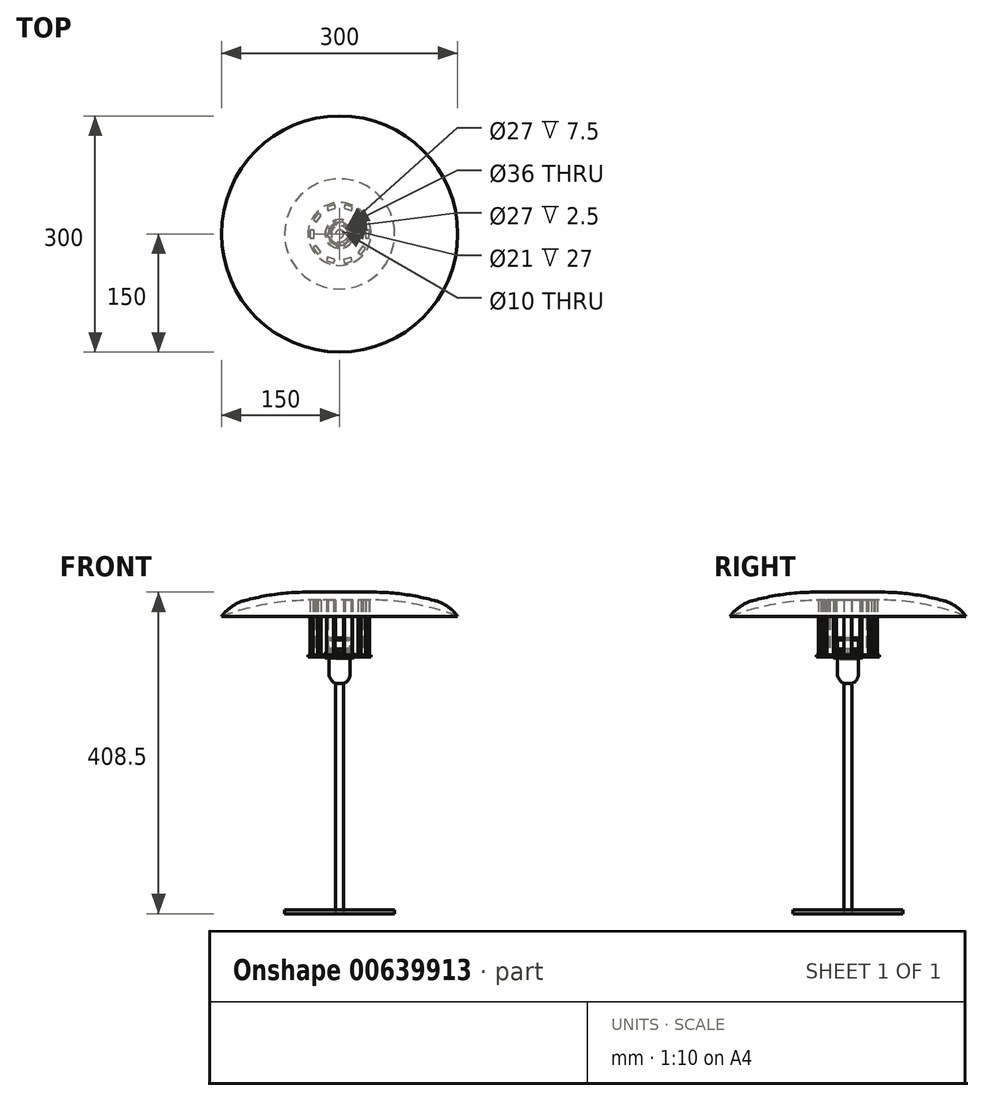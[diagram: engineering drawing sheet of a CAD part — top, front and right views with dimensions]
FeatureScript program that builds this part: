
annotation { "Feature Type Name" : "Feature", "Feature Type Description" : "" }
export const myFeature = defineFeature(function(context is Context, id is Id, definition is map)
    precondition{}
    {
        {
            var Q0;
            Q0=qCreatedBy(makeId("Top.planeOp"),FACE);
            var sketch = newSketch(context, id + "F0", { "sketchPlane" : qUnion([Q0])});
            skCircle(sketch, "E0", {"center": v(0, 0) * mm, "radius": 70 * mm});
            skSolve(sketch);
        }
        {
            var Q0;
            Q0=makeQuery(id+"F0.imprint","IMPRINT",FACE,{"disambiguationData":[TD([[makeQuery(id+"F0.imprint","IMPRINT",EDGE,{"derivedFrom":sQuery(id+"F0.wireOp",EDGE,"E0")}),1.0]])]});
            extrude(context, id + "F1", {"entities" : qUnion([Q0]), "depth" : 5 * mm, "offsetDistance" : 25 * mm});
        }
        {
            var Q0;
            Q0=makeQuery(id+"F1.opExtrude","CAP_FACE",FACE,{"disambiguationData":[OSD([sQuery(id+"F0.wireOp",EDGE,"E0")])],"isStart":false});
            var sketch = newSketch(context, id + "F2", { "sketchPlane" : qUnion([Q0])});
            skCircle(sketch, "E1", {"center": v(0, 0) * mm, "radius": 5 * mm});
            skSolve(sketch);
        }
        {
            var Q0;
            Q0=makeQuery(id+"F2.imprint","IMPRINT",FACE,{"disambiguationData":[TD([[makeQuery(id+"F2.imprint","IMPRINT",EDGE,{"derivedFrom":sQuery(id+"F2.wireOp",EDGE,"E1")}),1.0]])]});
            extrude(context, id + "F3", {"entities" : qUnion([Q0]), "operationType" : NewBodyOperationType.REMOVE, "endBound" : BoundingType.UP_TO_NEXT, "oppositeDirection" : true, "depth" : 25 * mm, "offsetDistance" : 25 * mm});
        }
        {
            var Q0;
            Q0=qCreatedBy(makeId("Top.planeOp"),FACE);
            var sketch = newSketch(context, id + "F4", { "sketchPlane" : qUnion([Q0])});
            skCircle(sketch, "E2", {"center": v(0, 0) * mm, "radius": 5 * mm});
            skSolve(sketch);
        }
        {
            var Q0;
            Q0=makeQuery(id+"F4.imprint","IMPRINT",FACE,{"disambiguationData":[TD([[makeQuery(id+"F4.imprint","IMPRINT",EDGE,{"derivedFrom":sQuery(id+"F4.wireOp",EDGE,"E2")}),1.0]])]});
            extrude(context, id + "F5", {"entities" : qUnion([Q0]), "depth" : 350 * mm, "offsetDistance" : 25 * mm});
        }
        {
            var Q0;
            Q0=qCreatedBy(makeId("Front.planeOp"),FACE);
            var sketch = newSketch(context, id + "F6", { "sketchPlane" : qUnion([Q0])});
            skLineSegment(sketch, "E3", {"start": v(0, 350) * mm, "end": v(13.5, 350) * mm});
            skLineSegment(sketch, "E4", {"start": v(13.5, 350) * mm, "end": v(13.5, 330.63) * mm});
            skLineSegment(sketch, "E5", {"start": v(13.5, 330.63) * mm, "end": v(13.5, 326) * mm});
            skLineSegment(sketch, "E6", {"start": v(13.5, 326) * mm, "end": v(18.5, 326) * mm});
            skLineSegment(sketch, "E7", {"start": v(18.5, 326) * mm, "end": v(18.5, 325) * mm});
            skLineSegment(sketch, "E8", {"start": v(18.5, 325) * mm, "end": v(13.5, 325) * mm});
            skLineSegment(sketch, "E9", {"start": v(13.5, 325) * mm, "end": v(13.5, 305) * mm});
            skArc(sketch, "E10", {"start": v(0, 291.5) * mm, "mid": v(9.55, 295.45) * mm, "end": v(13.5, 305) * mm});
            skLineSegment(sketch, "E11", {"start": v(0, 350) * mm, "end": v(0, 291.5) * mm});
            skSolve(sketch);
        }
        {
            var Q0;
            Q0=makeQuery(id+"F6.imprint","IMPRINT",FACE,{"disambiguationData":[TD([[makeQuery(id+"F6.imprint","IMPRINT",EDGE,{"derivedFrom":sQuery(id+"F6.wireOp",EDGE,"E3")}),-1.0]])]});
            var Q1;
            Q1=sQuery(id+"F6.wireOp",EDGE,"E11");
            revolve(context, id + "F7", {"operationType" : NewBodyOperationType.ADD, "entities" : qUnion([Q0]), "axis" : qUnion([Q1]), "revolveType" : RevolveType.FULL});
        }
        {
            var Q0;
            Q0=makeQuery(id+"F7.opRevolve","SWEPT_EDGE",EDGE,{"disambiguationData":[OSD([sQuery(id+"F6.wireOp",EDGE,"E6"),sQuery(id+"F6.wireOp",EDGE,"E7")])]});
            fillet(context, id + "F8", {"entities" : qUnion([Q0]), "radius" : 0.5 * mm, "tangentPropagation" : true, "allowEdgeOverflow" : false});
        }
        {
            var Q0;
            Q0=makeQuery(id+"F7.opRevolve","SWEPT_EDGE",EDGE,{"disambiguationData":[OSD([sQuery(id+"F6.wireOp",EDGE,"E7"),sQuery(id+"F6.wireOp",EDGE,"E8")])]});
            fillet(context, id + "F9", {"entities" : qUnion([Q0]), "radius" : 0.5 * mm, "tangentPropagation" : true, "allowEdgeOverflow" : false});
        }
        {
            var Q0;
            Q0=makeQuery(id+"F7.opRevolve","SWEPT_EDGE",EDGE,{"disambiguationData":[OSD([sQuery(id+"F6.wireOp",EDGE,"E3"),sQuery(id+"F6.wireOp",EDGE,"E4")])]});
            chamfer(context, id + "F10", {"entities" : qUnion([Q0]), "chamferType" : ChamferType.TWO_OFFSETS, "width1" : 1 * mm, "oppositeDirection" : false, "width2" : 2 * mm, "tangentPropagation" : true});
        }
        {
            var Q0;
            Q0=makeQuery(id+"F7.boolean.opBoolean","MERGE",FACE,{"derivedFrom":[makeQuery(id+"F5.opExtrude","CAP_FACE",FACE,{"disambiguationData":[OSD([sQuery(id+"F4.wireOp",EDGE,"E2")])],"isStart":false}),makeQuery(id+"F7.opRevolve","SWEPT_FACE",FACE,{"disambiguationData":[OSD([sQuery(id+"F6.wireOp",EDGE,"E3")])]})]});
            var sketch = newSketch(context, id + "F11", { "sketchPlane" : qUnion([Q0])});
            skCircle(sketch, "E12", {"center": v(0, 0) * mm, "radius": 10.5 * mm});
            skSolve(sketch);
        }
        {
            var Q0;
            Q0=makeQuery(id+"F11.imprint","IMPRINT",FACE,{"disambiguationData":[TD([[makeQuery(id+"F11.imprint","IMPRINT",EDGE,{"derivedFrom":sQuery(id+"F11.wireOp",EDGE,"E12")}),1.0]])]});
            extrude(context, id + "F12", {"entities" : qUnion([Q0]), "operationType" : NewBodyOperationType.REMOVE, "oppositeDirection" : true, "depth" : 27 * mm, "offsetDistance" : 25 * mm});
        }
        {
            var Q0;
            Q0=qCreatedBy(makeId("Front.planeOp"),FACE);
            var sketch = newSketch(context, id + "F13", { "sketchPlane" : qUnion([Q0])});
            skLineSegment(sketch, "E13", {"start": v(18, 329) * mm, "end": v(18, 331.5) * mm});
            skLineSegment(sketch, "E14", {"start": v(18, 331.5) * mm, "end": v(15.5, 331.5) * mm});
            skLineSegment(sketch, "E15", {"start": v(15.5, 331.5) * mm, "end": v(15.5, 336.5) * mm});
            skLineSegment(sketch, "E16", {"start": v(15.5, 336.5) * mm, "end": v(13.5, 336.5) * mm});
            skLineSegment(sketch, "E17", {"start": v(13.5, 336.5) * mm, "end": v(13.5, 329) * mm});
            skLineSegment(sketch, "E18", {"start": v(13.5, 329) * mm, "end": v(18, 329) * mm});
            skLineSegment(sketch, "E19", {"start": v(0, 351.5) * mm, "end": v(0, 305.84) * mm, "construction": true});
            skSolve(sketch);
        }
        {
            var Q0;
            Q0=makeQuery(id+"F13.imprint","IMPRINT",FACE,{"disambiguationData":[TD([[makeQuery(id+"F13.imprint","IMPRINT",EDGE,{"derivedFrom":sQuery(id+"F13.wireOp",EDGE,"E13")}),1.0]])]});
            var Q1;
            Q1=sQuery(id+"F13.wireOp",EDGE,"E19");
            revolve(context, id + "F14", {"entities" : qUnion([Q0]), "axis" : qUnion([Q1]), "revolveType" : RevolveType.FULL});
        }
        {
            var Q0;
            Q0=makeQuery(id+"F14.opRevolve","SWEPT_FACE",FACE,{"disambiguationData":[OSD([sQuery(id+"F13.wireOp",EDGE,"E16")])]});
            var sketch = newSketch(context, id + "F15", { "sketchPlane" : qUnion([Q0])});
            skArc(sketch, "E20", {"start": v(-15.5, 0) * mm, "mid": v(-15.16, 3.22) * mm, "end": v(-14.16, 6.3) * mm});
            skLineSegment(sketch, "E21", {"start": v(-14.16, 6.3) * mm, "end": v(0, 0) * mm});
            skLineSegment(sketch, "E22", {"start": v(-15.5, 0) * mm, "end": v(0, 0) * mm});
            skArc(sketch, "E23", {"start": v(-13.25, 5.9) * mm, "mid": v(-14.18, 3.01) * mm, "end": v(-14.5, 0) * mm});
            skArc(sketch, "E24.1.0", {"start": v(-14.18, -3.01) * mm, "mid": v(-13.25, -5.9) * mm, "end": v(-11.73, -8.52) * mm});
            skArc(sketch, "E24.1.1", {"start": v(-12.54, -9.11) * mm, "mid": v(-14.16, -6.3) * mm, "end": v(-15.16, -3.22) * mm});
            skLineSegment(sketch, "E24.1.2", {"start": v(-15.16, -3.22) * mm, "end": v(0, 0) * mm});
            skLineSegment(sketch, "E24.1.3", {"start": v(-12.54, -9.11) * mm, "end": v(0, 0) * mm});
            skArc(sketch, "E24.2.0", {"start": v(-9.7, -10.78) * mm, "mid": v(-7.25, -12.56) * mm, "end": v(-4.48, -13.8) * mm});
            skArc(sketch, "E24.2.1", {"start": v(-4.79, -14.74) * mm, "mid": v(-7.75, -13.42) * mm, "end": v(-10.37, -11.52) * mm});
            skLineSegment(sketch, "E24.2.2", {"start": v(-10.37, -11.52) * mm, "end": v(0, 0) * mm});
            skLineSegment(sketch, "E24.2.3", {"start": v(-4.79, -14.74) * mm, "end": v(0, 0) * mm});
            skArc(sketch, "E24.3.0", {"start": v(-1.52, -14.42) * mm, "mid": v(1.52, -14.42) * mm, "end": v(4.48, -13.8) * mm});
            skArc(sketch, "E24.3.1", {"start": v(4.79, -14.74) * mm, "mid": v(1.62, -15.42) * mm, "end": v(-1.62, -15.42) * mm});
            skLineSegment(sketch, "E24.3.2", {"start": v(-1.62, -15.42) * mm, "end": v(0, 0) * mm});
            skLineSegment(sketch, "E24.3.3", {"start": v(4.79, -14.74) * mm, "end": v(0, 0) * mm});
            skArc(sketch, "E24.4.0", {"start": v(7.25, -12.56) * mm, "mid": v(9.7, -10.78) * mm, "end": v(11.73, -8.52) * mm});
            skArc(sketch, "E24.4.1", {"start": v(12.54, -9.11) * mm, "mid": v(10.37, -11.52) * mm, "end": v(7.75, -13.42) * mm});
            skLineSegment(sketch, "E24.4.2", {"start": v(7.75, -13.42) * mm, "end": v(0, 0) * mm});
            skLineSegment(sketch, "E24.4.3", {"start": v(12.54, -9.11) * mm, "end": v(0, 0) * mm});
            skArc(sketch, "E24.5.0", {"start": v(13.25, -5.9) * mm, "mid": v(14.18, -3.01) * mm, "end": v(14.5, 0) * mm});
            skArc(sketch, "E24.5.1", {"start": v(15.5, 0) * mm, "mid": v(15.16, -3.22) * mm, "end": v(14.16, -6.3) * mm});
            skLineSegment(sketch, "E24.5.2", {"start": v(14.16, -6.3) * mm, "end": v(0, 0) * mm});
            skLineSegment(sketch, "E24.5.3", {"start": v(15.5, 0) * mm, "end": v(0, 0) * mm});
            skArc(sketch, "E24.6.0", {"start": v(14.18, 3.01) * mm, "mid": v(13.25, 5.9) * mm, "end": v(11.73, 8.52) * mm});
            skArc(sketch, "E24.6.1", {"start": v(12.54, 9.11) * mm, "mid": v(14.16, 6.3) * mm, "end": v(15.16, 3.22) * mm});
            skLineSegment(sketch, "E24.6.2", {"start": v(15.16, 3.22) * mm, "end": v(0, 0) * mm});
            skLineSegment(sketch, "E24.6.3", {"start": v(12.54, 9.11) * mm, "end": v(0, 0) * mm});
            skArc(sketch, "E24.7.0", {"start": v(9.7, 10.78) * mm, "mid": v(7.25, 12.56) * mm, "end": v(4.48, 13.8) * mm});
            skArc(sketch, "E24.7.1", {"start": v(4.79, 14.74) * mm, "mid": v(7.75, 13.42) * mm, "end": v(10.37, 11.52) * mm});
            skLineSegment(sketch, "E24.7.2", {"start": v(10.37, 11.52) * mm, "end": v(0, 0) * mm});
            skLineSegment(sketch, "E24.7.3", {"start": v(4.79, 14.74) * mm, "end": v(0, 0) * mm});
            skArc(sketch, "E24.8.0", {"start": v(1.52, 14.42) * mm, "mid": v(-1.52, 14.42) * mm, "end": v(-4.48, 13.8) * mm});
            skArc(sketch, "E24.8.1", {"start": v(-4.79, 14.74) * mm, "mid": v(-1.62, 15.42) * mm, "end": v(1.62, 15.42) * mm});
            skLineSegment(sketch, "E24.8.2", {"start": v(1.62, 15.42) * mm, "end": v(0, 0) * mm});
            skLineSegment(sketch, "E24.8.3", {"start": v(-4.79, 14.74) * mm, "end": v(0, 0) * mm});
            skArc(sketch, "E24.9.0", {"start": v(-7.25, 12.56) * mm, "mid": v(-9.7, 10.78) * mm, "end": v(-11.73, 8.52) * mm});
            skArc(sketch, "E24.9.1", {"start": v(-12.54, 9.11) * mm, "mid": v(-10.37, 11.52) * mm, "end": v(-7.75, 13.42) * mm});
            skLineSegment(sketch, "E24.9.2", {"start": v(-7.75, 13.42) * mm, "end": v(0, 0) * mm});
            skLineSegment(sketch, "E24.9.3", {"start": v(-12.54, 9.11) * mm, "end": v(0, 0) * mm});
            skSolve(sketch);
        }
        {
            var Q0;
            {var subQ0=sQuery(id+"F15.wireOp",EDGE,"E20");Q0=makeQuery(id+"F15.imprint","IMPRINT",FACE,{"disambiguationData":[TD([[makeQuery(id+"F15.imprint","IMPRINT",EDGE,{"derivedFrom":subQ0}),1.0]])]});}
            var Q1;
            {var subQ0=sQuery(id+"F15.wireOp",EDGE,"E24.9.0");Q1=makeQuery(id+"F15.imprint","IMPRINT",FACE,{"disambiguationData":[TD([[makeQuery(id+"F15.imprint","IMPRINT",EDGE,{"derivedFrom":subQ0}),-1.0]])]});}
            var Q2;
            {var subQ0=sQuery(id+"F15.wireOp",EDGE,"E24.8.0");Q2=makeQuery(id+"F15.imprint","IMPRINT",FACE,{"disambiguationData":[TD([[makeQuery(id+"F15.imprint","IMPRINT",EDGE,{"derivedFrom":subQ0}),-1.0]])]});}
            var Q3;
            {var subQ0=sQuery(id+"F15.wireOp",EDGE,"E24.7.0");Q3=makeQuery(id+"F15.imprint","IMPRINT",FACE,{"disambiguationData":[TD([[makeQuery(id+"F15.imprint","IMPRINT",EDGE,{"derivedFrom":subQ0}),-1.0]])]});}
            var Q4;
            {var subQ0=sQuery(id+"F15.wireOp",EDGE,"E24.6.0");Q4=makeQuery(id+"F15.imprint","IMPRINT",FACE,{"disambiguationData":[TD([[makeQuery(id+"F15.imprint","IMPRINT",EDGE,{"derivedFrom":subQ0}),-1.0]])]});}
            var Q5;
            {var subQ0=sQuery(id+"F15.wireOp",EDGE,"E24.5.0");Q5=makeQuery(id+"F15.imprint","IMPRINT",FACE,{"disambiguationData":[TD([[makeQuery(id+"F15.imprint","IMPRINT",EDGE,{"derivedFrom":subQ0}),-1.0]])]});}
            var Q6;
            {var subQ0=sQuery(id+"F15.wireOp",EDGE,"E24.4.0");Q6=makeQuery(id+"F15.imprint","IMPRINT",FACE,{"disambiguationData":[TD([[makeQuery(id+"F15.imprint","IMPRINT",EDGE,{"derivedFrom":subQ0}),-1.0]])]});}
            var Q7;
            {var subQ0=sQuery(id+"F15.wireOp",EDGE,"E24.3.0");Q7=makeQuery(id+"F15.imprint","IMPRINT",FACE,{"disambiguationData":[TD([[makeQuery(id+"F15.imprint","IMPRINT",EDGE,{"derivedFrom":subQ0}),-1.0]])]});}
            var Q8;
            {var subQ0=sQuery(id+"F15.wireOp",EDGE,"E24.2.0");Q8=makeQuery(id+"F15.imprint","IMPRINT",FACE,{"disambiguationData":[TD([[makeQuery(id+"F15.imprint","IMPRINT",EDGE,{"derivedFrom":subQ0}),-1.0]])]});}
            var Q9;
            {var subQ0=sQuery(id+"F15.wireOp",EDGE,"E24.1.0");Q9=makeQuery(id+"F15.imprint","IMPRINT",FACE,{"disambiguationData":[TD([[makeQuery(id+"F15.imprint","IMPRINT",EDGE,{"derivedFrom":subQ0}),-1.0]])]});}
            extrude(context, id + "F16", {"entities" : qUnion([Q0, Q1, Q2, Q3, Q4, Q5, Q6, Q7, Q8, Q9]), "operationType" : NewBodyOperationType.REMOVE, "oppositeDirection" : true, "depth" : 5 * mm, "offsetDistance" : 25 * mm});
        }
        {
            var Q0;
            Q0=makeQuery(id+"F7.opRevolve","SWEPT_FACE",FACE,{"disambiguationData":[OSD([sQuery(id+"F6.wireOp",EDGE,"E6")])]});
            var sketch = newSketch(context, id + "F17", { "sketchPlane" : qUnion([Q0])});
            skCircle(sketch, "E25", {"center": v(0, 0) * mm, "radius": 13.5 * mm});
            skCircle(sketch, "E26", {"center": v(0, 0) * mm, "radius": 40 * mm});
            skSolve(sketch);
        }
        {
            var Q0;
            Q0=makeQuery(id+"F17.imprint","IMPRINT",FACE,{"disambiguationData":[TD([[makeQuery(id+"F17.imprint","IMPRINT",EDGE,{"derivedFrom":sQuery(id+"F17.wireOp",EDGE,"E26")}),1.0]])]});
            extrude(context, id + "F18", {"entities" : qUnion([Q0]), "depth" : 2.5 * mm, "offsetDistance" : 25 * mm});
        }
        {
            var Q0;
            Q0=makeQuery(id+"F18.opExtrude","CAP_FACE",FACE,{"disambiguationData":[OSD([sQuery(id+"F6.wireOp",EDGE,"E6"),sQuery(id+"F6.wireOp",EDGE,"E7"),sQuery(id+"F17.wireOp",EDGE,"E26")])],"isStart":false});
            var sketch = newSketch(context, id + "F19", { "sketchPlane" : qUnion([Q0])});
            skLineSegment(sketch, "E27", {"start": v(-37.67, 5) * mm, "end": v(-37.67, -5) * mm});
            skLineSegment(sketch, "E28", {"start": v(-37.67, -5) * mm, "end": v(-32.67, -5) * mm});
            skLineSegment(sketch, "E29", {"start": v(-32.67, -5) * mm, "end": v(-32.67, 5) * mm});
            skLineSegment(sketch, "E30", {"start": v(-32.67, 5) * mm, "end": v(-37.67, 5) * mm});
            skCircle(sketch, "E31", {"center": v(0, 0) * mm, "radius": 38 * mm, "construction": true});
            skLineSegment(sketch, "E32.1.0", {"start": v(-23.45, 23.3) * mm, "end": v(-27.49, 26.24) * mm});
            skLineSegment(sketch, "E32.1.1", {"start": v(-29.34, 15.21) * mm, "end": v(-23.45, 23.3) * mm});
            skLineSegment(sketch, "E32.1.2", {"start": v(-33.38, 18.16) * mm, "end": v(-29.34, 15.21) * mm});
            skLineSegment(sketch, "E32.1.3", {"start": v(-27.49, 26.24) * mm, "end": v(-33.38, 18.16) * mm});
            skLineSegment(sketch, "E32.2.0", {"start": v(-5.21, 32.64) * mm, "end": v(-6.74, 37.4) * mm});
            skLineSegment(sketch, "E32.2.1", {"start": v(-14.74, 29.58) * mm, "end": v(-5.21, 32.64) * mm});
            skLineSegment(sketch, "E32.2.2", {"start": v(-16.26, 34.34) * mm, "end": v(-14.74, 29.58) * mm});
            skLineSegment(sketch, "E32.2.3", {"start": v(-6.74, 37.4) * mm, "end": v(-16.26, 34.34) * mm});
            skLineSegment(sketch, "E32.3.0", {"start": v(15.02, 29.44) * mm, "end": v(16.6, 34.18) * mm});
            skLineSegment(sketch, "E32.3.1", {"start": v(5.53, 32.58) * mm, "end": v(15.02, 29.44) * mm});
            skLineSegment(sketch, "E32.3.2", {"start": v(7.1, 37.33) * mm, "end": v(5.53, 32.58) * mm});
            skLineSegment(sketch, "E32.3.3", {"start": v(16.6, 34.18) * mm, "end": v(7.1, 37.33) * mm});
            skLineSegment(sketch, "E32.4.0", {"start": v(29.49, 14.93) * mm, "end": v(33.55, 17.84) * mm});
            skLineSegment(sketch, "E32.4.1", {"start": v(23.67, 23.06) * mm, "end": v(29.49, 14.93) * mm});
            skLineSegment(sketch, "E32.4.2", {"start": v(27.74, 25.97) * mm, "end": v(23.67, 23.06) * mm});
            skLineSegment(sketch, "E32.4.3", {"start": v(33.55, 17.84) * mm, "end": v(27.74, 25.97) * mm});
            skLineSegment(sketch, "E32.5.0", {"start": v(32.62, -5.32) * mm, "end": v(37.62, -5.37) * mm});
            skLineSegment(sketch, "E32.5.1", {"start": v(32.72, 4.68) * mm, "end": v(32.62, -5.32) * mm});
            skLineSegment(sketch, "E32.5.2", {"start": v(37.72, 4.63) * mm, "end": v(32.72, 4.68) * mm});
            skLineSegment(sketch, "E32.5.3", {"start": v(37.62, -5.37) * mm, "end": v(37.72, 4.63) * mm});
            skLineSegment(sketch, "E32.6.0", {"start": v(23.22, -23.52) * mm, "end": v(27.23, -26.5) * mm});
            skLineSegment(sketch, "E32.6.1", {"start": v(29.2, -15.5) * mm, "end": v(23.22, -23.52) * mm});
            skLineSegment(sketch, "E32.6.2", {"start": v(33.2, -18.48) * mm, "end": v(29.2, -15.5) * mm});
            skLineSegment(sketch, "E32.6.3", {"start": v(27.23, -26.5) * mm, "end": v(33.2, -18.48) * mm});
            skLineSegment(sketch, "E32.7.0", {"start": v(4.9, -32.69) * mm, "end": v(6.38, -37.46) * mm});
            skLineSegment(sketch, "E32.7.1", {"start": v(14.45, -29.72) * mm, "end": v(4.9, -32.69) * mm});
            skLineSegment(sketch, "E32.7.2", {"start": v(15.93, -34.5) * mm, "end": v(14.45, -29.72) * mm});
            skLineSegment(sketch, "E32.7.3", {"start": v(6.38, -37.46) * mm, "end": v(15.93, -34.5) * mm});
            skLineSegment(sketch, "E32.8.0", {"start": v(-15.3, -29.3) * mm, "end": v(-16.93, -34.02) * mm});
            skLineSegment(sketch, "E32.8.1", {"start": v(-5.85, -32.53) * mm, "end": v(-15.3, -29.3) * mm});
            skLineSegment(sketch, "E32.8.2", {"start": v(-7.46, -37.26) * mm, "end": v(-5.85, -32.53) * mm});
            skLineSegment(sketch, "E32.8.3", {"start": v(-16.93, -34.02) * mm, "end": v(-7.46, -37.26) * mm});
            skLineSegment(sketch, "E32.9.0", {"start": v(-29.63, -14.64) * mm, "end": v(-33.73, -17.51) * mm});
            skLineSegment(sketch, "E32.9.1", {"start": v(-23.9, -22.83) * mm, "end": v(-29.63, -14.64) * mm});
            skLineSegment(sketch, "E32.9.2", {"start": v(-27.99, -25.7) * mm, "end": v(-23.9, -22.83) * mm});
            skLineSegment(sketch, "E32.9.3", {"start": v(-33.73, -17.51) * mm, "end": v(-27.99, -25.7) * mm});
            skLineSegment(sketch, "E32.anchor1", {"start": v(0, 0) * mm, "end": v(-37.67, 5) * mm, "construction": true});
            skLineSegment(sketch, "E32.anchor2", {"start": v(0, 0) * mm, "end": v(-33.73, -17.51) * mm, "construction": true});
            skSolve(sketch);
        }
        {
            var Q0;
            Q0=makeQuery(id+"F19.imprint","IMPRINT",FACE,{"disambiguationData":[TD([[makeQuery(id+"F19.imprint","IMPRINT",EDGE,{"derivedFrom":sQuery(id+"F19.wireOp",EDGE,"E32.9.0")}),1.0]])]});
            var Q1;
            Q1=makeQuery(id+"F19.imprint","IMPRINT",FACE,{"disambiguationData":[TD([[makeQuery(id+"F19.imprint","IMPRINT",EDGE,{"derivedFrom":sQuery(id+"F19.wireOp",EDGE,"E27")}),1.0]])]});
            var Q2;
            Q2=makeQuery(id+"F19.imprint","IMPRINT",FACE,{"disambiguationData":[TD([[makeQuery(id+"F19.imprint","IMPRINT",EDGE,{"derivedFrom":sQuery(id+"F19.wireOp",EDGE,"E32.1.0")}),1.0]])]});
            var Q3;
            Q3=makeQuery(id+"F19.imprint","IMPRINT",FACE,{"disambiguationData":[TD([[makeQuery(id+"F19.imprint","IMPRINT",EDGE,{"derivedFrom":sQuery(id+"F19.wireOp",EDGE,"E32.2.0")}),1.0]])]});
            var Q4;
            Q4=makeQuery(id+"F19.imprint","IMPRINT",FACE,{"disambiguationData":[TD([[makeQuery(id+"F19.imprint","IMPRINT",EDGE,{"derivedFrom":sQuery(id+"F19.wireOp",EDGE,"E32.3.0")}),1.0]])]});
            var Q5;
            Q5=makeQuery(id+"F19.imprint","IMPRINT",FACE,{"disambiguationData":[TD([[makeQuery(id+"F19.imprint","IMPRINT",EDGE,{"derivedFrom":sQuery(id+"F19.wireOp",EDGE,"E32.4.0")}),1.0]])]});
            var Q6;
            Q6=makeQuery(id+"F19.imprint","IMPRINT",FACE,{"disambiguationData":[TD([[makeQuery(id+"F19.imprint","IMPRINT",EDGE,{"derivedFrom":sQuery(id+"F19.wireOp",EDGE,"E32.5.0")}),1.0]])]});
            var Q7;
            Q7=makeQuery(id+"F19.imprint","IMPRINT",FACE,{"disambiguationData":[TD([[makeQuery(id+"F19.imprint","IMPRINT",EDGE,{"derivedFrom":sQuery(id+"F19.wireOp",EDGE,"E32.6.0")}),1.0]])]});
            var Q8;
            Q8=makeQuery(id+"F19.imprint","IMPRINT",FACE,{"disambiguationData":[TD([[makeQuery(id+"F19.imprint","IMPRINT",EDGE,{"derivedFrom":sQuery(id+"F19.wireOp",EDGE,"E32.7.0")}),1.0]])]});
            var Q9;
            Q9=makeQuery(id+"F19.imprint","IMPRINT",FACE,{"disambiguationData":[TD([[makeQuery(id+"F19.imprint","IMPRINT",EDGE,{"derivedFrom":sQuery(id+"F19.wireOp",EDGE,"E32.8.0")}),1.0]])]});
            extrude(context, id + "F20", {"entities" : qUnion([Q0, Q1, Q2, Q3, Q4, Q5, Q6, Q7, Q8, Q9]), "operationType" : NewBodyOperationType.ADD, "depth" : 70 * mm, "offsetDistance" : 25 * mm});
        }
        {
            var Q0;
            Q0=qCreatedBy(makeId("Front.planeOp"),FACE);
            var sketch = newSketch(context, id + "F21", { "sketchPlane" : qUnion([Q0])});
            skLineSegment(sketch, "E33", {"start": v(0, 398.5) * mm, "end": v(40, 398.5) * mm});
            skArc(sketch, "E34", {"start": v(150, 377.6) * mm, "mid": v(95.98, 393.23) * mm, "end": v(40, 398.5) * mm});
            skLineSegment(sketch, "E35.0", {"start": v(0, 408.5) * mm, "end": v(40, 408.5) * mm});
            skArc(sketch, "E35.1", {"start": v(120.41, 397.89) * mm, "mid": v(80.56, 405.84) * mm, "end": v(40, 408.5) * mm});
            skArc(sketch, "E36", {"start": v(150, 377.6) * mm, "mid": v(136.94, 390.28) * mm, "end": v(120.41, 397.89) * mm});
            skLineSegment(sketch, "E37", {"start": v(0, 408.5) * mm, "end": v(0, 398.5) * mm});
            skSolve(sketch);
        }
        {
            var Q0;
            Q0=makeQuery(id+"F21.imprint","IMPRINT",FACE,{"disambiguationData":[TD([[makeQuery(id+"F21.imprint","IMPRINT",EDGE,{"derivedFrom":sQuery(id+"F21.wireOp",EDGE,"E33")}),1.0]])]});
            var Q1;
            Q1=sQuery(id+"F21.wireOp",EDGE,"E37");
            revolve(context, id + "F22", {"entities" : qUnion([Q0]), "axis" : qUnion([Q1]), "revolveType" : RevolveType.FULL});
        }
        {
            var Q0;
            Q0=makeQuery(id+"F7.opRevolve","SWEPT_FACE",FACE,{"disambiguationData":[OSD([sQuery(id+"F6.wireOp",EDGE,"E6")])]});
            extrude(context, id + "F23", {"entities" : qUnion([Q0]), "depth" : 2.5 * mm, "offsetDistance" : 25 * mm});
        }
    });
